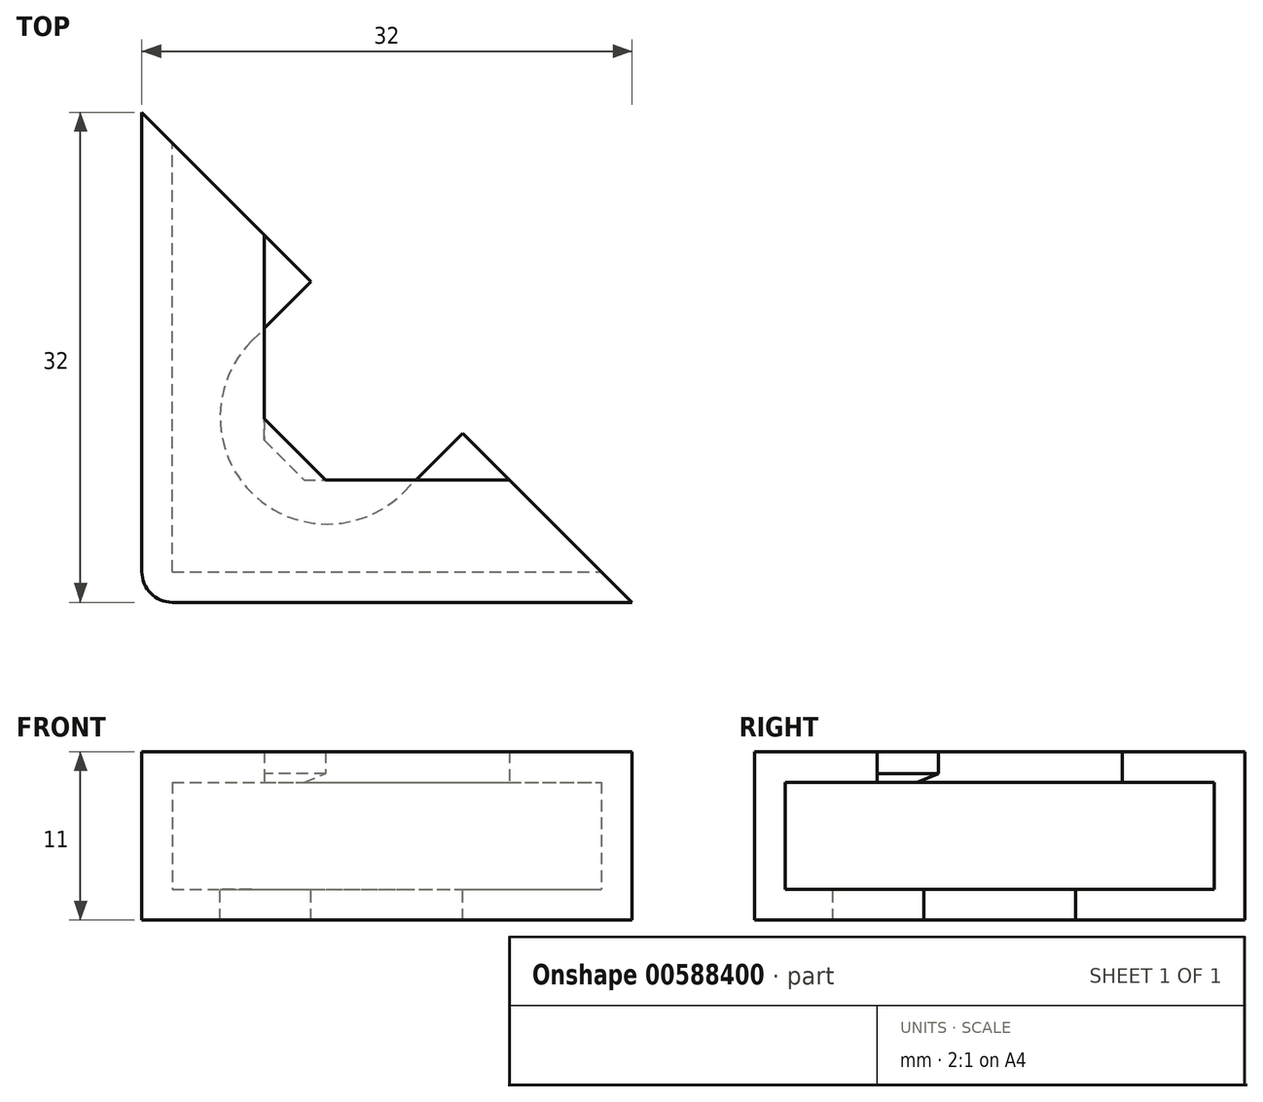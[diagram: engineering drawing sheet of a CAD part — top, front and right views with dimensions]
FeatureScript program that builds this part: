
annotation { "Feature Type Name" : "Feature", "Feature Type Description" : "" }
export const myFeature = defineFeature(function(context is Context, id is Id, definition is map)
    precondition{}
    {
        {
            var Q0;
            Q0=qCreatedBy(makeId("Top.planeOp"),FACE);
            var sketch = newSketch(context, id + "F0", { "sketchPlane" : qUnion([Q0])});
            skLineSegment(sketch, "E0", {"start": v(0, 0) * mm, "end": v(0, 32) * mm});
            skLineSegment(sketch, "E1", {"start": v(0, 0) * mm, "end": v(32, 0) * mm});
            skLineSegment(sketch, "E2", {"start": v(0, 32) * mm, "end": v(32, 0) * mm});
            skSolve(sketch);
        }
        {
            var Q0;
            Q0 = qSketchRegion(id + "F0", true);
            extrude(context, id + "F1", {"entities" : qUnion([Q0]), "depth" : 2 * mm, "offsetDistance" : 25 * mm});
        }
        {
            var Q0;
            Q0=makeQuery(id+"F1.opExtrude","CAP_FACE",FACE,{"disambiguationData":[OSD([sQuery(id+"F0.wireOp",EDGE,"E0"),sQuery(id+"F0.wireOp",EDGE,"E1"),sQuery(id+"F0.wireOp",EDGE,"E2")])],"isStart":false});
            var sketch = newSketch(context, id + "F2", { "sketchPlane" : qUnion([Q0])});
            skLineSegment(sketch, "E3", {"start": v(0, 0) * mm, "end": v(16, 16) * mm, "construction": true});
            skLineSegment(sketch, "E4.0", {"start": v(7.16, 17.06) * mm, "end": v(11.05, 20.95) * mm});
            skLineSegment(sketch, "E5.0", {"start": v(4.95, -4.95) * mm, "end": v(20.95, 11.05) * mm, "construction": true});
            skArc(sketch, "E6", {"start": v(7.16, 17.06) * mm, "mid": v(7.16, 7.16) * mm, "end": v(17.06, 7.16) * mm});
            skLineSegment(sketch, "E7", {"start": v(17.06, 7.16) * mm, "end": v(20.95, 11.05) * mm});
            skSolve(sketch);
        }
        {
            var Q0;
            Q0 = qSketchRegion(id + "F2", true);
            var Q1;
            {var subQ0=sQuery(id+"F2.wireOp",EDGE,"E4.0");Q1=makeQuery(id+"F2.imprint","IMPRINT",FACE,{"disambiguationData":[TD([[makeQuery(id+"F2.imprint","IMPRINT",EDGE,{"derivedFrom":subQ0}),-1.0]])]});}
            extrude(context, id + "F3", {"entities" : qUnion([Q0, Q1]), "operationType" : NewBodyOperationType.REMOVE, "oppositeDirection" : true, "depth" : 25 * mm, "offsetDistance" : 25 * mm});
        }
        {
            var Q0;
            Q0=makeQuery(id+"F1.opExtrude","CAP_FACE",FACE,{"disambiguationData":[OSD([sQuery(id+"F0.wireOp",EDGE,"E0"),sQuery(id+"F0.wireOp",EDGE,"E1"),sQuery(id+"F0.wireOp",EDGE,"E2")])],"isStart":false});
            var sketch = newSketch(context, id + "F4", { "sketchPlane" : qUnion([Q0])});
            skLineSegment(sketch, "E8.0", {"start": v(0, 0) * mm, "end": v(0, 32) * mm});
            skLineSegment(sketch, "E9.0", {"start": v(0, 0) * mm, "end": v(32, 0) * mm});
            skLineSegment(sketch, "E10.0", {"start": v(2, 2) * mm, "end": v(2, 30) * mm});
            skLineSegment(sketch, "E11.0", {"start": v(2, 2) * mm, "end": v(30, 2) * mm});
            skLineSegment(sketch, "E12.0", {"start": v(0, 32) * mm, "end": v(2, 30) * mm});
            skLineSegment(sketch, "E13.0", {"start": v(30, 2) * mm, "end": v(32, 0) * mm});
            skPoint(sketch, "E14.orphan", {"position": v(11.05, 20.95) * mm});
            skPoint(sketch, "E15.orphan", {"position": v(20.95, 11.05) * mm});
            skSolve(sketch);
        }
        {
            var Q0;
            Q0 = qSketchRegion(id + "F4", true);
            extrude(context, id + "F5", {"entities" : qUnion([Q0]), "operationType" : NewBodyOperationType.ADD, "depth" : 7 * mm, "offsetDistance" : 25 * mm});
        }
        {
            var Q0;
            Q0=makeQuery(id+"F5.opExtrude","CAP_FACE",FACE,{"disambiguationData":[OSD([sQuery(id+"F4.wireOp",EDGE,"E8.0"),sQuery(id+"F4.wireOp",EDGE,"E9.0"),sQuery(id+"F4.wireOp",EDGE,"E10.0"),sQuery(id+"F4.wireOp",EDGE,"E11.0"),sQuery(id+"F4.wireOp",EDGE,"E12.0"),sQuery(id+"F4.wireOp",EDGE,"E13.0")])],"isStart":false});
            var sketch = newSketch(context, id + "F6", { "sketchPlane" : qUnion([Q0])});
            skLineSegment(sketch, "E16.0", {"start": v(0, 0) * mm, "end": v(0, 32) * mm});
            skLineSegment(sketch, "E17.0", {"start": v(0, 0) * mm, "end": v(32, 0) * mm});
            skLineSegment(sketch, "E18", {"start": v(8, 12) * mm, "end": v(12, 8) * mm});
            skLineSegment(sketch, "E19", {"start": v(0, 32) * mm, "end": v(2, 30) * mm});
            skLineSegment(sketch, "E20.0", {"start": v(8, 12) * mm, "end": v(8, 24) * mm});
            skLineSegment(sketch, "E21", {"start": v(2, 30) * mm, "end": v(8, 24) * mm});
            skLineSegment(sketch, "E22.0", {"start": v(12, 8) * mm, "end": v(24, 8) * mm});
            skLineSegment(sketch, "E23", {"start": v(32, 0) * mm, "end": v(30, 2) * mm});
            skLineSegment(sketch, "E24", {"start": v(30, 2) * mm, "end": v(24, 8) * mm});
            skPoint(sketch, "E25.orphan", {"position": v(20, 0) * mm});
            skSolve(sketch);
        }
        {
            var Q0;
            Q0 = qSketchRegion(id + "F6", true);
            extrude(context, id + "F7", {"entities" : qUnion([Q0]), "operationType" : NewBodyOperationType.ADD, "depth" : 2 * mm, "offsetDistance" : 25 * mm});
        }
        {
            var Q0;
            {var subQ0=sQuery(id+"F6.wireOp",EDGE,"E18");Q0=makeQuery(id+"F7.boolean.opBoolean","SPLIT",EDGE,{"disambiguationData":[topologyDisambiguationEdgeConnected([makeQuery(id+"F7.opExtrude","CAP_FACE",FACE,{"disambiguationData":[OSD([sQuery(id+"F6.wireOp",EDGE,"E16.0"),sQuery(id+"F6.wireOp",EDGE,"E17.0"),subQ0])],"isStart":true}),makeQuery(id+"F7.opExtrude","SWEPT_FACE",FACE,{"disambiguationData":[OSD([subQ0])]})])],"derivedFrom":makeQuery(id+"F7.opExtrude","CAP_EDGE",EDGE,{"disambiguationData":[OSD([subQ0])],"isStart":true})});}
            chamfer(context, id + "F8", {"entities" : qUnion([Q0]), "chamferType" : ChamferType.OFFSET_ANGLE, "width" : 1 * mm, "oppositeDirection" : false, "angle" : 30 * degree, "tangentPropagation" : true});
        }
        {
            var Q0;
            Q0=makeQuery(id+"F7.boolean.opBoolean","MERGE",EDGE,{"derivedFrom":[makeQuery(id+"F5.boolean.opBoolean","MERGE",EDGE,{"derivedFrom":[makeQuery(id+"F1.opExtrude","SWEPT_EDGE",EDGE,{"disambiguationData":[OSD([sQuery(id+"F0.wireOp",EDGE,"E0"),sQuery(id+"F0.wireOp",EDGE,"E1")])]}),makeQuery(id+"F5.opExtrude","SWEPT_EDGE",EDGE,{"disambiguationData":[OSD([sQuery(id+"F4.wireOp",EDGE,"E8.0"),sQuery(id+"F4.wireOp",EDGE,"E9.0")])]})]}),makeQuery(id+"F7.opExtrude","SWEPT_EDGE",EDGE,{"disambiguationData":[OSD([sQuery(id+"F6.wireOp",EDGE,"E16.0"),sQuery(id+"F6.wireOp",EDGE,"E17.0")])]})]});
            fillet(context, id + "F9", {"entities" : qUnion([Q0]), "radius" : 2 * mm, "tangentPropagation" : true, "allowEdgeOverflow" : false});
        }
    });
